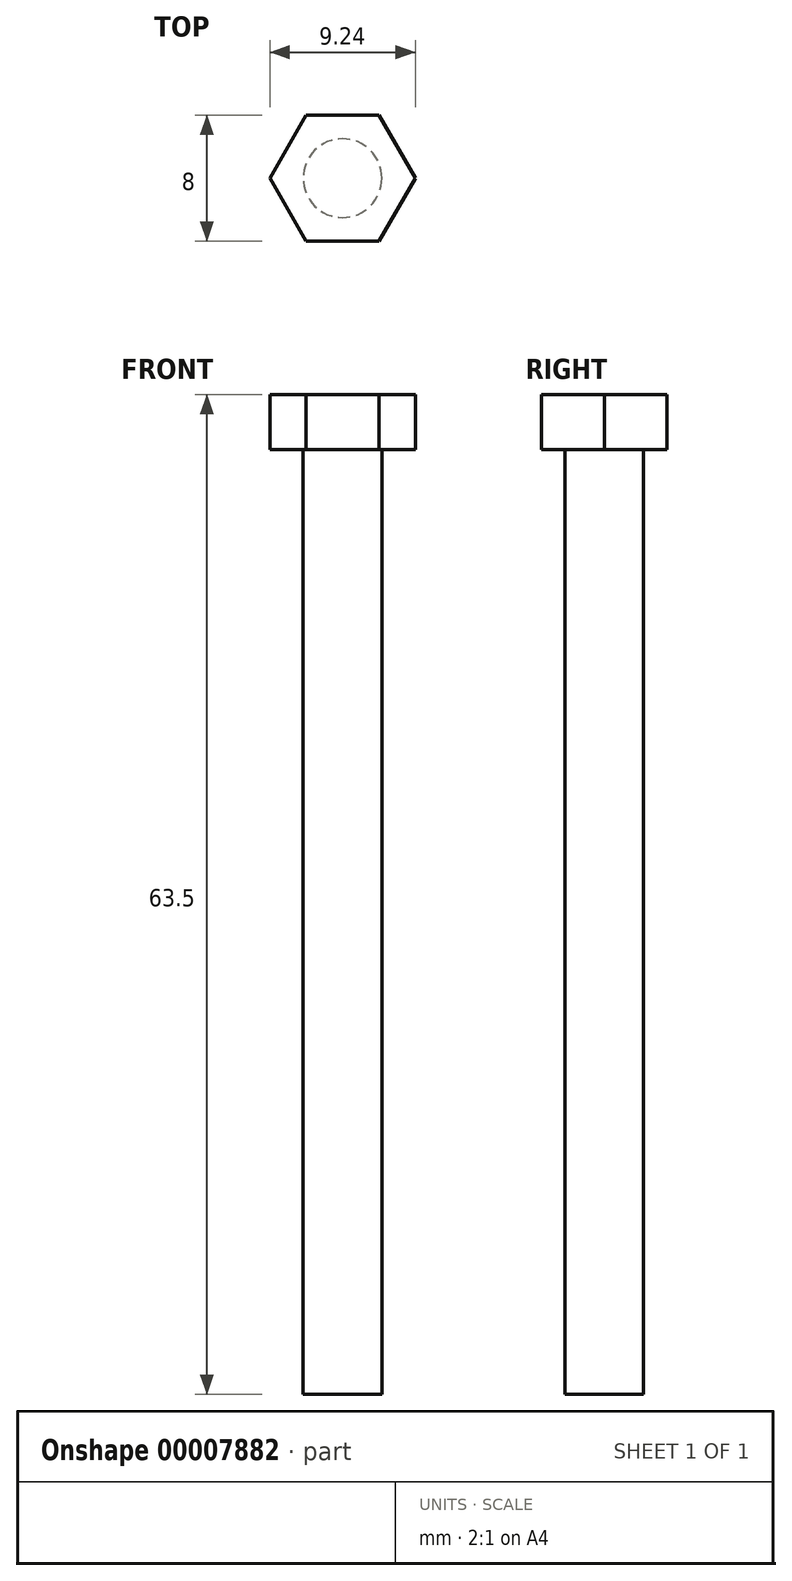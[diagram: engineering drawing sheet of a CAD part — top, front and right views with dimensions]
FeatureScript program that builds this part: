
annotation { "Feature Type Name" : "Feature", "Feature Type Description" : "" }
export const myFeature = defineFeature(function(context is Context, id is Id, definition is map)
    precondition{}
    {
        {
            var Q0;
            Q0=qCreatedBy(makeId("Top.planeOp"),FACE);
            var sketch = newSketch(context, id + "F0", { "sketchPlane" : qUnion([Q0])});
            skCircle(sketch, "E0.cCircle", {"center": v(0, 0) * mm, "radius": 4 * mm, "construction": true});
            skLineSegment(sketch, "E0.0", {"start": v(-2.3, 4) * mm, "end": v(2.3, 4) * mm});
            skLineSegment(sketch, "E0.1", {"start": v(2.3, 4) * mm, "end": v(4.62, 0) * mm});
            skLineSegment(sketch, "E0.2", {"start": v(4.62, 0) * mm, "end": v(2.3, -4) * mm});
            skLineSegment(sketch, "E0.3", {"start": v(2.3, -4) * mm, "end": v(-2.3, -4) * mm});
            skLineSegment(sketch, "E0.4", {"start": v(-2.3, -4) * mm, "end": v(-4.62, 0) * mm});
            skLineSegment(sketch, "E0.5", {"start": v(-4.62, 0) * mm, "end": v(-2.3, 4) * mm});
            skPoint(sketch, "E0.0.midPoint", {"position": v(0, 4) * mm});
            skSolve(sketch);
        }
        {
            var Q0;
            Q0=makeQuery(id+"F0.imprint","IMPRINT",FACE,{"disambiguationData":[TD([[makeQuery(id+"F0.imprint","IMPRINT",EDGE,{"derivedFrom":sQuery(id+"F0.wireOp",EDGE,"E0.0")}),-1.0]])]});
            extrude(context, id + "F1", {"entities" : qUnion([Q0]), "depth" : 3.5 * mm});
        }
        {
            var Q0;
            Q0=qCreatedBy(makeId("Top.planeOp"),FACE);
            var sketch = newSketch(context, id + "F2", { "sketchPlane" : qUnion([Q0])});
            skCircle(sketch, "E1", {"center": v(0, 0) * mm, "radius": 2.5 * mm});
            skSolve(sketch);
        }
        {
            var Q0;
            Q0 = qSketchRegion(id + "F2", true);
            extrude(context, id + "F3", {"entities" : qUnion([Q0]), "operationType" : NewBodyOperationType.ADD, "oppositeDirection" : true, "depth" : 60 * mm});
        }
    });
